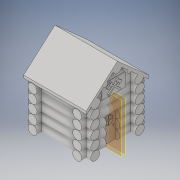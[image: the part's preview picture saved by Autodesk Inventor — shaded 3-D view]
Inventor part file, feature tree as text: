
AUTODESK INVENTOR PART (.ipt)
format: ipt  version: 2018 (Build 220112000, 112)  size: 879,104 bytes
history: native  units: in
note: dims shown in document units (in); Inventor stores cm internally (conversion verified against a paired STEP export)
features: extrude x15, sketch x15, plane x7, mirror x5, chamfer x2, projected_geometry x2, fillet x1
ambient origin geometry x8: Origin, YZ Plane, XZ Plane, XY Plane, X Axis, Y Axis, Z Axis, Center Point
bodies: Solid1 (feature_tree)
feature tree (47):
  extrude  "Extrusion1"  Depth=2.5in
  extrude  "Extrusion2"  Depth=3.5in
  extrude  "Extrusion3"  Depth=0.25in
  sketch  "Sketch4"  dims[d7=0.5in d8=0.5in]
  plane  "Work Plane1"
  mirror  "Mirror1"
  plane  "Work Plane4"
  extrude  "Extrusion4"  Depth=0.5in
  mirror  "Mirror2"
  mirror  "Mirror3"
  plane  "Work Plane7"
  sketch  "Sketch8"  dims[d11=0.25in d12=0.25in]
  extrude  "Extrusion6"  Depth=0.25in
  extrude  "Extrusion7"  Depth=0.25in
  extrude  "Extrusion8"  Depth=0.25in TaperAngle=0.0deg
  mirror  "Mirror4"
  plane  "Work Plane5"
  mirror  "Mirror5"
  plane  "Work Plane6"
  extrude  "Extrusion9"  Depth=0.25in
  extrude  "Extrusion10"  Depth=1.75in
  extrude  "Extrusion11"  Depth=0.25in
  extrude  "Extrusion12"  Depth=0.25in
  extrude  "Extrusion13"  Depth=0.25in
  extrude  "Extrusion14"  Depth=3.5in TaperAngle=0.0deg
  fillet  "Fillet1"  Radius=0.125in
  extrude  "Extrusion15"  TaperAngle=0.0deg  [1 undecoded]
  chamfer  "Chamfer1"  Distance=0.2in
  chamfer  "Chamfer2"  Distance=0.15in
  plane  "Work Plane8"
  extrude  "Extrusion16"  Depth=0.125in
  sketch  "Sketch1"  dims[d0=3.0in d1=2.5in]
  sketch  "Sketch2"  dims[d2=3.5in d3=0.0in d4=0.5in]
  sketch  "Sketch3"  dims[d5=90.0deg d6=0.25in]
  projected_geometry  "Projected Loop1"
  plane  "Work Plane3"
  sketch  "Sketch5"  dims[d9=0.5in d10=0.25in]
  projected_geometry  "Projected Loop2"
  sketch  "Sketch9"  dims[d13=0.25in d14=4.0in d15=0.0in]
  sketch  "Sketch10"  dims[d16=0.25in d17=0.25in]
  sketch  "Sketch11"  dims[d18=0.5in d19=0.0in d20=1.75in]
  sketch  "Sketch12"  dims[d21=0.25in d22=0.25in]
  sketch  "Sketch13"  dims[d23=0.5in d24=0.25in]
  sketch  "Sketch14"  dims[d25=0.25in d26=0.25in]
  sketch  "Sketch15"  dims[d27=0.25in d28=3.5in d29=0.0in d39=0.125in]
  sketch  "Sketch17"  dims[d40=0.125in d42=0.0in]
  sketch  "Sketch19"  dims[d43=0.2in d44=0.2in d45=0.15in d46=0.5in d47=0.136in d48=0.5in d49=0.0in d50=0.34in d51=0.25in d53=1.2in d54=3.5in d55=0.0in d56=3.5in d57=0.0in d58=0.5in d59=0.25in d60=0.5in d61=0.25in d64=0.168in d65=0.168in d66=0.1684in d67=0.25in d68=0.0in d69=1.0in d70=0.0in d71=0.25in d72=-0.225in d73=1.2in d74=1.2in d75=0.85in d76=0.75in d77=1.0in d78=0.0in d79=0.075in d80=0.0375in d81=0.35in d82=0.12in d83=0.15in d84=0.2in d85=0.125in d86=0.3779in d87=0.8921in d88=0.56in d89=0.0in d90=0.0in d91=0.0375in d92=0.575in d93=0.0625in d94=0.0in d96=1.375in d97=1.5in d98=0.75in d99=0.275in d100=0.0in d101=0.5in d102=0.05in d103=0.025in d104=0.375in d105=0.025in d106=0.025in d107=0.4in d108=0.3in d109=0.0in d110=0.08in d111=0.75in d112=0.1in d113=0.1in d114=0.0in d115=0.11in d116=0.07in d117=0.0in d118=0.04in d119=1.0in d120=0.0in d121=0.2in d122=0.125in d123=45.0deg d124=0.1645in d125=0.125in d126=45.0deg d127=0.2in d128=1.0in d129=0.0in]
note: 1 required parameter value undecoded (feature->parameter linkage not recoverable at this tier; creation-order binding heuristic only, values carry confidence <= 0.55)
